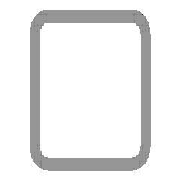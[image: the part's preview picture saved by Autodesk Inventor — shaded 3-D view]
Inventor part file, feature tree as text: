
AUTODESK INVENTOR PART (.ipt)
format: ipt  version: 2025 (Build 290162010, 162A)  size: 133,120 bytes
history: native  units: mm (DEFAULTED — no unit token found)
features: other x4, sketch x1, plane x1
ambient origin geometry x8: Origin, YZ Plane, XZ Plane, XY Plane, X Axis, Y Axis, Z Axis, Center Point
bodies: Solid1 (feature_tree), Body (feature_tree)
feature tree (6):
  parser-record x1  (decoder bookkeeping rows leaked as tree rows — omitted from the tree; the rows remain in map.json)
  other  "Driven Length"
  other  "Start Plane"
  other  "End Plane"
  sketch  "Sketch3"  dims[d3=2600.0mm d4=0.0mm d7=6.0mm d9=100.0mm d11=100.0mm d12=3.0mm d13=-0.0mm d14=2600.0mm d15=50.0mm d16=50.0mm d17=90.0deg d18=2600.0mm]
  plane  "Work Plane3"
